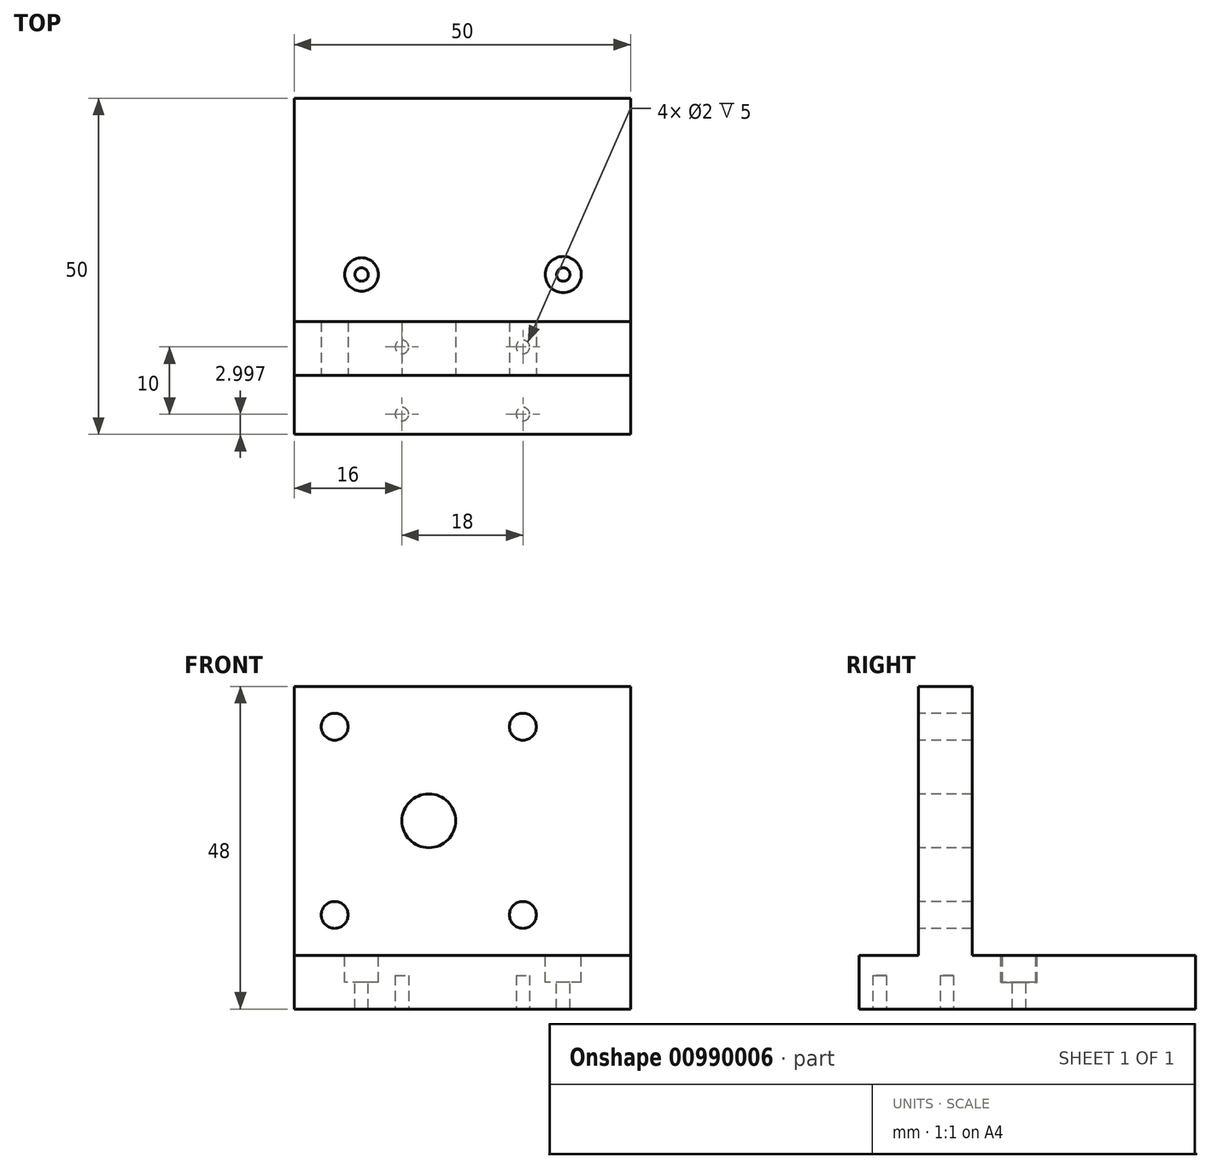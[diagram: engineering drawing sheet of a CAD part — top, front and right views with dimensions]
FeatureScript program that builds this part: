
annotation { "Feature Type Name" : "Feature", "Feature Type Description" : "" }
export const myFeature = defineFeature(function(context is Context, id is Id, definition is map)
    precondition{}
    {
        {
            var Q0;
            Q0=qCreatedBy(makeId("Right.planeOp"),FACE);
            var sketch = newSketch(context, id + "F0", { "sketchPlane" : qUnion([Q0])});
            skLineSegment(sketch, "E0", {"start": v(41.23, 0) * mm, "end": v(41.23, 8) * mm});
            skLineSegment(sketch, "E1", {"start": v(41.23, 8) * mm, "end": v(8, 8) * mm});
            skLineSegment(sketch, "E2", {"start": v(8, 8) * mm, "end": v(8, 48) * mm});
            skLineSegment(sketch, "E3", {"start": v(8, 48) * mm, "end": v(0, 48) * mm});
            skLineSegment(sketch, "E4", {"start": v(0, 48) * mm, "end": v(0, 8) * mm});
            skLineSegment(sketch, "E5", {"start": v(0, 8) * mm, "end": v(-8.77, 8) * mm});
            skLineSegment(sketch, "E6", {"start": v(-8.77, 8) * mm, "end": v(-8.77, 0) * mm});
            skLineSegment(sketch, "E7", {"start": v(41.23, 0) * mm, "end": v(-8.77, 0) * mm});
            skSolve(sketch);
        }
        {
            var Q0;
            Q0=makeQuery(id+"F0.imprint","IMPRINT",FACE,{"disambiguationData":[TD([[makeQuery(id+"F0.imprint","IMPRINT",EDGE,{"derivedFrom":sQuery(id+"F0.wireOp",EDGE,"E0")}),1.0]])]});
            extrude(context, id + "F1", {"entities" : qUnion([Q0]), "depth" : 50 * mm, "offsetDistance" : 25 * mm});
        }
        {
            var Q0;
            Q0=makeQuery(id+"F1.opExtrude","SWEPT_FACE",FACE,{"disambiguationData":[OSD([sQuery(id+"F0.wireOp",EDGE,"E4")])]});
            var sketch = newSketch(context, id + "F2", { "sketchPlane" : qUnion([Q0])});
            skLineSegment(sketch, "E8", {"start": v(25, 48) * mm, "end": v(25, 8) * mm, "construction": true});
            skCircle(sketch, "E9", {"center": v(20, 28) * mm, "radius": 4 * mm});
            skLineSegment(sketch, "E10.bottom", {"start": v(34, 42) * mm, "end": v(6, 42) * mm, "construction": true});
            skLineSegment(sketch, "E10.top", {"start": v(34, 14) * mm, "end": v(6, 14) * mm, "construction": true});
            skLineSegment(sketch, "E10.left", {"start": v(34, 42) * mm, "end": v(34, 14) * mm, "construction": true});
            skLineSegment(sketch, "E10.right", {"start": v(6, 42) * mm, "end": v(6, 14) * mm, "construction": true});
            skCircle(sketch, "E11", {"center": v(6, 42) * mm, "radius": 2 * mm});
            skCircle(sketch, "E12", {"center": v(34, 42) * mm, "radius": 2 * mm});
            skCircle(sketch, "E13", {"center": v(34, 14) * mm, "radius": 2 * mm});
            skCircle(sketch, "E14", {"center": v(6, 14) * mm, "radius": 2 * mm});
            skSolve(sketch);
        }
        {
            var Q0;
            Q0=makeQuery(id+"F2.imprint","IMPRINT",FACE,{"disambiguationData":[TD([[makeQuery(id+"F2.imprint","IMPRINT",EDGE,{"derivedFrom":sQuery(id+"F2.wireOp",EDGE,"E11")}),1.0]])]});
            var Q1;
            Q1=makeQuery(id+"F2.imprint","IMPRINT",FACE,{"disambiguationData":[TD([[makeQuery(id+"F2.imprint","IMPRINT",EDGE,{"derivedFrom":sQuery(id+"F2.wireOp",EDGE,"E14")}),1.0]])]});
            var Q2;
            Q2=makeQuery(id+"F2.imprint","IMPRINT",FACE,{"disambiguationData":[TD([[makeQuery(id+"F2.imprint","IMPRINT",EDGE,{"derivedFrom":sQuery(id+"F2.wireOp",EDGE,"E9")}),1.0]])]});
            var Q3;
            Q3=makeQuery(id+"F2.imprint","IMPRINT",FACE,{"disambiguationData":[TD([[makeQuery(id+"F2.imprint","IMPRINT",EDGE,{"derivedFrom":sQuery(id+"F2.wireOp",EDGE,"E12")}),1.0]])]});
            var Q4;
            Q4=makeQuery(id+"F2.imprint","IMPRINT",FACE,{"disambiguationData":[TD([[makeQuery(id+"F2.imprint","IMPRINT",EDGE,{"derivedFrom":sQuery(id+"F2.wireOp",EDGE,"E13")}),1.0]])]});
            extrude(context, id + "F3", {"entities" : qUnion([Q0, Q1, Q2, Q3, Q4]), "operationType" : NewBodyOperationType.REMOVE, "endBound" : BoundingType.UP_TO_NEXT, "oppositeDirection" : true, "depth" : 25 * mm, "offsetDistance" : 25 * mm});
        }
        {
            var Q0;
            Q0=makeQuery(id+"F1.opExtrude","SWEPT_FACE",FACE,{"disambiguationData":[OSD([sQuery(id+"F0.wireOp",EDGE,"E7")])]});
            var sketch = newSketch(context, id + "F4", { "sketchPlane" : qUnion([Q0])});
            skLineSegment(sketch, "E15", {"start": v(25, 8.77) * mm, "end": v(25, -41.23) * mm, "construction": true});
            skLineSegment(sketch, "E16.bottom", {"start": v(16, -4.23) * mm, "end": v(34, -4.23) * mm, "construction": true});
            skLineSegment(sketch, "E16.top", {"start": v(16, 5.77) * mm, "end": v(34, 5.77) * mm, "construction": true});
            skLineSegment(sketch, "E16.left", {"start": v(16, -4.23) * mm, "end": v(16, 5.77) * mm, "construction": true});
            skLineSegment(sketch, "E16.right", {"start": v(34, -4.23) * mm, "end": v(34, 5.77) * mm, "construction": true});
            skPoint(sketch, "E16.middle", {"position": v(25, 0.77) * mm});
            skCircle(sketch, "E17", {"center": v(16, 5.77) * mm, "radius": 1 * mm});
            skCircle(sketch, "E18", {"center": v(34, 5.77) * mm, "radius": 1 * mm});
            skCircle(sketch, "E19", {"center": v(34, -4.23) * mm, "radius": 1 * mm});
            skCircle(sketch, "E20", {"center": v(16, -4.23) * mm, "radius": 1 * mm});
            skSolve(sketch);
        }
        {
            var Q0;
            Q0=makeQuery(id+"F4.imprint","IMPRINT",FACE,{"disambiguationData":[TD([[makeQuery(id+"F4.imprint","IMPRINT",EDGE,{"derivedFrom":sQuery(id+"F4.wireOp",EDGE,"E17")}),1.0]])]});
            var Q1;
            Q1=makeQuery(id+"F4.imprint","IMPRINT",FACE,{"disambiguationData":[TD([[makeQuery(id+"F4.imprint","IMPRINT",EDGE,{"derivedFrom":sQuery(id+"F4.wireOp",EDGE,"E18")}),1.0]])]});
            var Q2;
            Q2=makeQuery(id+"F4.imprint","IMPRINT",FACE,{"disambiguationData":[TD([[makeQuery(id+"F4.imprint","IMPRINT",EDGE,{"derivedFrom":sQuery(id+"F4.wireOp",EDGE,"E19")}),1.0]])]});
            var Q3;
            Q3=makeQuery(id+"F4.imprint","IMPRINT",FACE,{"disambiguationData":[TD([[makeQuery(id+"F4.imprint","IMPRINT",EDGE,{"derivedFrom":sQuery(id+"F4.wireOp",EDGE,"E20")}),1.0]])]});
            extrude(context, id + "F5", {"entities" : qUnion([Q0, Q1, Q2, Q3]), "operationType" : NewBodyOperationType.REMOVE, "oppositeDirection" : true, "depth" : 5 * mm, "offsetDistance" : 25 * mm});
        }
        {
            var Q0;
            Q0=makeQuery(id+"F1.opExtrude","SWEPT_FACE",FACE,{"disambiguationData":[OSD([sQuery(id+"F0.wireOp",EDGE,"E1")])]});
            var sketch = newSketch(context, id + "F6", { "sketchPlane" : qUnion([Q0])});
            skLineSegment(sketch, "E21", {"start": v(25, 41.23) * mm, "end": v(25, 8) * mm, "construction": true});
            skCircle(sketch, "E22", {"center": v(10, 15) * mm, "radius": 1 * mm});
            skCircle(sketch, "E23", {"center": v(10, 15) * mm, "radius": 2.5 * mm});
            skCircle(sketch, "E24", {"center": v(40, 15) * mm, "radius": 1 * mm});
            skCircle(sketch, "E25", {"center": v(40, 15) * mm, "radius": 2.5 * mm});
            skLineSegment(sketch, "E26", {"start": v(10, 15) * mm, "end": v(25, 15) * mm, "construction": true});
            skLineSegment(sketch, "E27", {"start": v(40, 15) * mm, "end": v(25, 15) * mm, "construction": true});
            skSolve(sketch);
        }
        {
            var Q0;
            Q0=makeQuery(id+"F6.imprint","IMPRINT",FACE,{"disambiguationData":[TD([[makeQuery(id+"F6.imprint","IMPRINT",EDGE,{"derivedFrom":sQuery(id+"F6.wireOp",EDGE,"E22")}),1.0]])]});
            var Q1;
            Q1=makeQuery(id+"F6.imprint","IMPRINT",FACE,{"disambiguationData":[TD([[makeQuery(id+"F6.imprint","IMPRINT",EDGE,{"derivedFrom":sQuery(id+"F6.wireOp",EDGE,"E24")}),1.0]])]});
            extrude(context, id + "F7", {"entities" : qUnion([Q0, Q1]), "operationType" : NewBodyOperationType.REMOVE, "endBound" : BoundingType.UP_TO_NEXT, "oppositeDirection" : true, "depth" : 25 * mm, "offsetDistance" : 25 * mm});
        }
        {
            var Q0;
            Q0=makeQuery(id+"F1.opExtrude","SWEPT_FACE",FACE,{"disambiguationData":[OSD([sQuery(id+"F0.wireOp",EDGE,"E1")])]});
            var sketch = newSketch(context, id + "F8", { "sketchPlane" : qUnion([Q0])});
            skCircle(sketch, "E28", {"center": v(10, 15) * mm, "radius": 2.5 * mm});
            skCircle(sketch, "E29", {"center": v(40, 15) * mm, "radius": 2.69 * mm});
            skSolve(sketch);
        }
        {
            var Q0;
            Q0=makeQuery(id+"F8.imprint","IMPRINT",FACE,{"disambiguationData":[TD([[makeQuery(id+"F8.imprint","IMPRINT",EDGE,{"derivedFrom":sQuery(id+"F8.wireOp",EDGE,"E28")}),1.0]])]});
            var Q1;
            Q1=makeQuery(id+"F8.imprint","IMPRINT",FACE,{"disambiguationData":[TD([[makeQuery(id+"F8.imprint","IMPRINT",EDGE,{"derivedFrom":sQuery(id+"F8.wireOp",EDGE,"E29")}),1.0]])]});
            extrude(context, id + "F9", {"entities" : qUnion([Q0, Q1]), "operationType" : NewBodyOperationType.REMOVE, "oppositeDirection" : true, "depth" : 4 * mm, "offsetDistance" : 25 * mm});
        }
    });
